# Revit family: Diverter_Rough_In Valve-American_Standard-Flash-RU531_Series
name_source: partatom
category: Pipe Accessories
units: mm (PartAtom-declared; Revit-internal decimal feet)

## family parameters
Cut with Voids When Loaded = No
Host = Face
OmniClass Number = 23.65.55.14
OmniClass Title = Valves for Liquid Services
Part Type = Normal
Round Connector Dimension = Use Diameter
Shared = Yes

## types (2) — shared parameters
ADA Compliant = Yes
Assembly Code = D2020
CW Connection = Yes
CWFU = 3
Compliance Certifications = These products meet or exceed the following codes and standards: ASSE 101, ASME A112.18.1, CSA B125.1
Default Elevation = 0"
Description = Flash® 3-Way Integrated Shower Diverter Rough-In Valve with Pressure Balance Valve Cartridge
Finish = Metal-American Standard-Brass
HW Connection = Yes
HWFU = 3
Inlet Connection Diameter = 1/2"
Installation Type = Recessed Wall Mounted
Manufacturer = American Standard
Material = Metal-American Standard-Brass
Outlet Connection Diameter = 1/2"
Product Documentation Link = https://americanstandard.box.com
Product Page URL = https://www.americanstandard-us.com
URL = https://www.americanstandard-us.com
Vent Connection = No
WFU = 4
Waste Connection = No
Width = 4 7/8"

## per-type parameters (varying)
| type | 2-Way Shared cartridge #M970720-0070A (sold separately) | Type Comments |
| RU531 (Discrete) | No |  |
| RU531 (Shared) | Yes | Note: Shared functionality requires the RU531 rough valve, plus the 3-Way Shared cartridge #M970730-0070A (sold separately) |

note: column(s) folded — value = type name in every type: Model

## geometry (parser evidence)
native form markers: Sweep x3
no freeform markers — native parametric forms only
